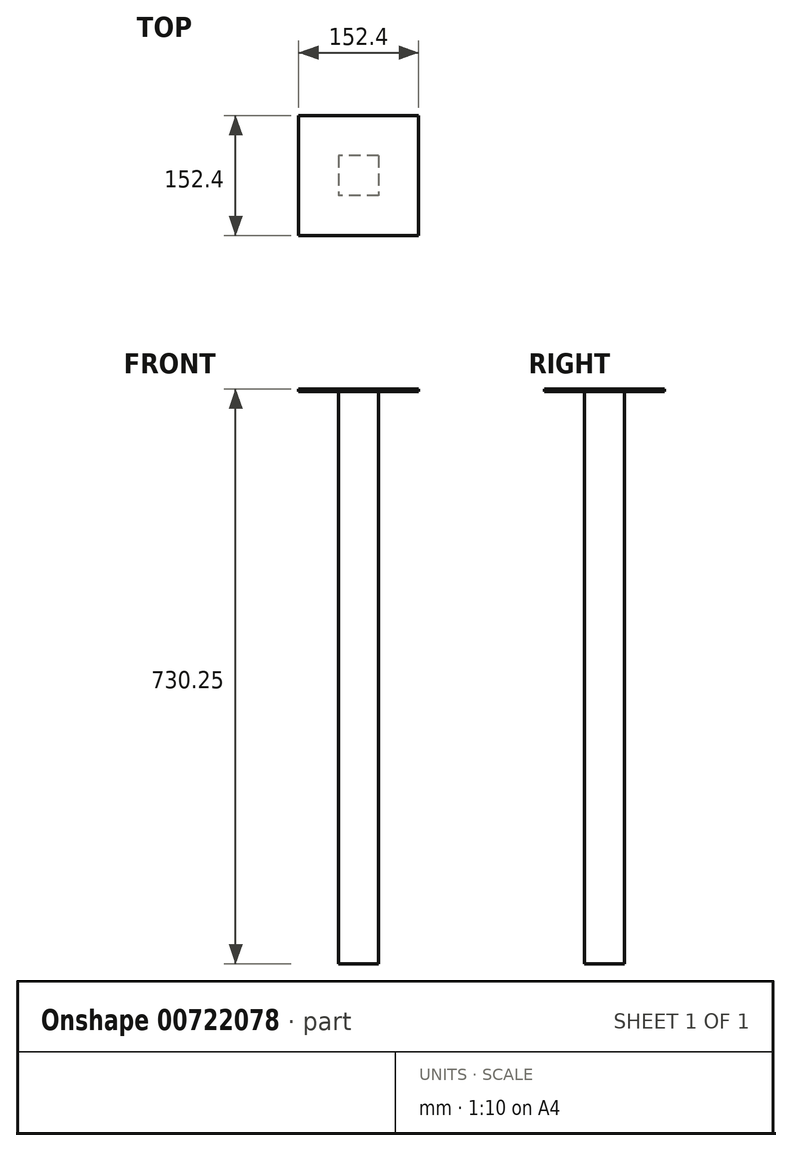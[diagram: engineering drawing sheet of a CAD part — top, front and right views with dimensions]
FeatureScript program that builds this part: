
annotation { "Feature Type Name" : "Feature", "Feature Type Description" : "" }
export const myFeature = defineFeature(function(context is Context, id is Id, definition is map)
    precondition{}
    {
        {
            var Q0;
            Q0=qCreatedBy(makeId("Top.planeOp"),FACE);
            var sketch = newSketch(context, id + "F0", { "sketchPlane" : qUnion([Q0])});
            skLineSegment(sketch, "E0.bottom", {"start": v(25.4, 25.4) * mm, "end": v(-25.4, 25.4) * mm});
            skLineSegment(sketch, "E0.top", {"start": v(25.4, -25.4) * mm, "end": v(-25.4, -25.4) * mm});
            skLineSegment(sketch, "E0.left", {"start": v(25.4, 25.4) * mm, "end": v(25.4, -25.4) * mm});
            skLineSegment(sketch, "E0.right", {"start": v(-25.4, 25.4) * mm, "end": v(-25.4, -25.4) * mm});
            skPoint(sketch, "E0.middle", {"position": v(0, 0) * mm});
            skSolve(sketch);
        }
        {
            var Q0;
            Q0=makeQuery(id+"F0.imprint","IMPRINT",FACE,{"disambiguationData":[TD([[makeQuery(id+"F0.imprint","IMPRINT",EDGE,{"derivedFrom":sQuery(id+"F0.wireOp",EDGE,"E0.bottom")}),1.0]])]});
            extrude(context, id + "F1", {"entities" : qUnion([Q0]), "depth" : 727.07 * mm, "offsetDistance" : 25.4 * mm});
        }
        {
            var Q0;
            Q0=makeQuery(id+"F1.opExtrude","CAP_FACE",FACE,{"disambiguationData":[OSD([sQuery(id+"F0.wireOp",EDGE,"E0.bottom"),sQuery(id+"F0.wireOp",EDGE,"E0.top"),sQuery(id+"F0.wireOp",EDGE,"E0.left"),sQuery(id+"F0.wireOp",EDGE,"E0.right")])],"isStart":false});
            var sketch = newSketch(context, id + "F2", { "sketchPlane" : qUnion([Q0])});
            skLineSegment(sketch, "E1.bottom", {"start": v(76.2, 76.2) * mm, "end": v(-76.2, 76.2) * mm});
            skLineSegment(sketch, "E1.top", {"start": v(76.2, -76.2) * mm, "end": v(-76.2, -76.2) * mm});
            skLineSegment(sketch, "E1.left", {"start": v(76.2, 76.2) * mm, "end": v(76.2, -76.2) * mm});
            skLineSegment(sketch, "E1.right", {"start": v(-76.2, 76.2) * mm, "end": v(-76.2, -76.2) * mm});
            skPoint(sketch, "E1.middle", {"position": v(0, 0) * mm});
            skSolve(sketch);
        }
        {
            var Q0;
            Q0=makeQuery(id+"F2.imprint","IMPRINT",FACE,{"disambiguationData":[TD([[makeQuery(id+"F2.imprint","IMPRINT",EDGE,{"derivedFrom":sQuery(id+"F2.wireOp",EDGE,"E1.bottom")}),1.0]])]});
            var Q1;
            Q1=makeQuery(id+"F2.imprint","IMPRINT",FACE,{"disambiguationData":[TD([[makeQuery(id+"F2.imprint","IMPRINT",EDGE,{"derivedFrom":makeQuery(id+"F1.opExtrude","CAP_EDGE",EDGE,{"disambiguationData":[OSD([sQuery(id+"F0.wireOp",EDGE,"E0.bottom")])],"isStart":false})}),1.0]])]});
            extrude(context, id + "F3", {"entities" : qUnion([Q0, Q1]), "operationType" : NewBodyOperationType.ADD, "depth" : 3.17 * mm, "offsetDistance" : 25.4 * mm});
        }
    });
